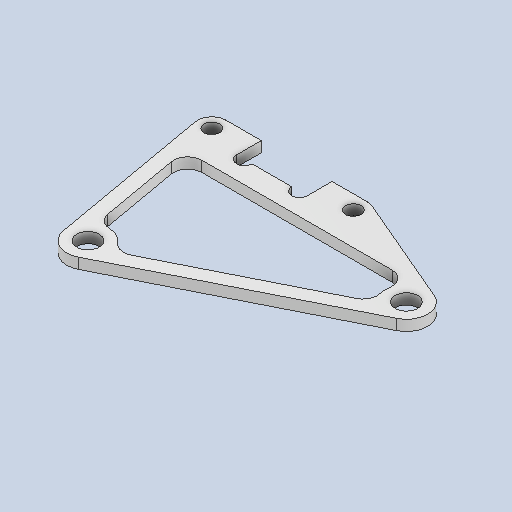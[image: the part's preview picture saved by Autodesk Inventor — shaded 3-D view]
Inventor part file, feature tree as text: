
AUTODESK INVENTOR PART (.ipt)
format: ipt  version: 2025.1 (Build 291241000, 241)  size: 233,984 bytes
history: native  units: mm
features: extrude x2, sketch x2, other x1, fillet x1, projected_geometry x1
ambient origin geometry x8: Origin, YZ Plane, XZ Plane, XY Plane, X Axis, Y Axis, Z Axis, Center Point
bodies: Body1 (feature_tree)
feature tree (7):
  other  "ソリッド1"
  extrude  "押し出し1"  Depth=10.0mm
  extrude  "押し出し2"  Depth=3.0mm
  fillet  "フィレット1"  Radius=2.2mm
  sketch  "スケッチ1"
  sketch  "スケッチ2"
  projected_geometry  "投影ループ1"
